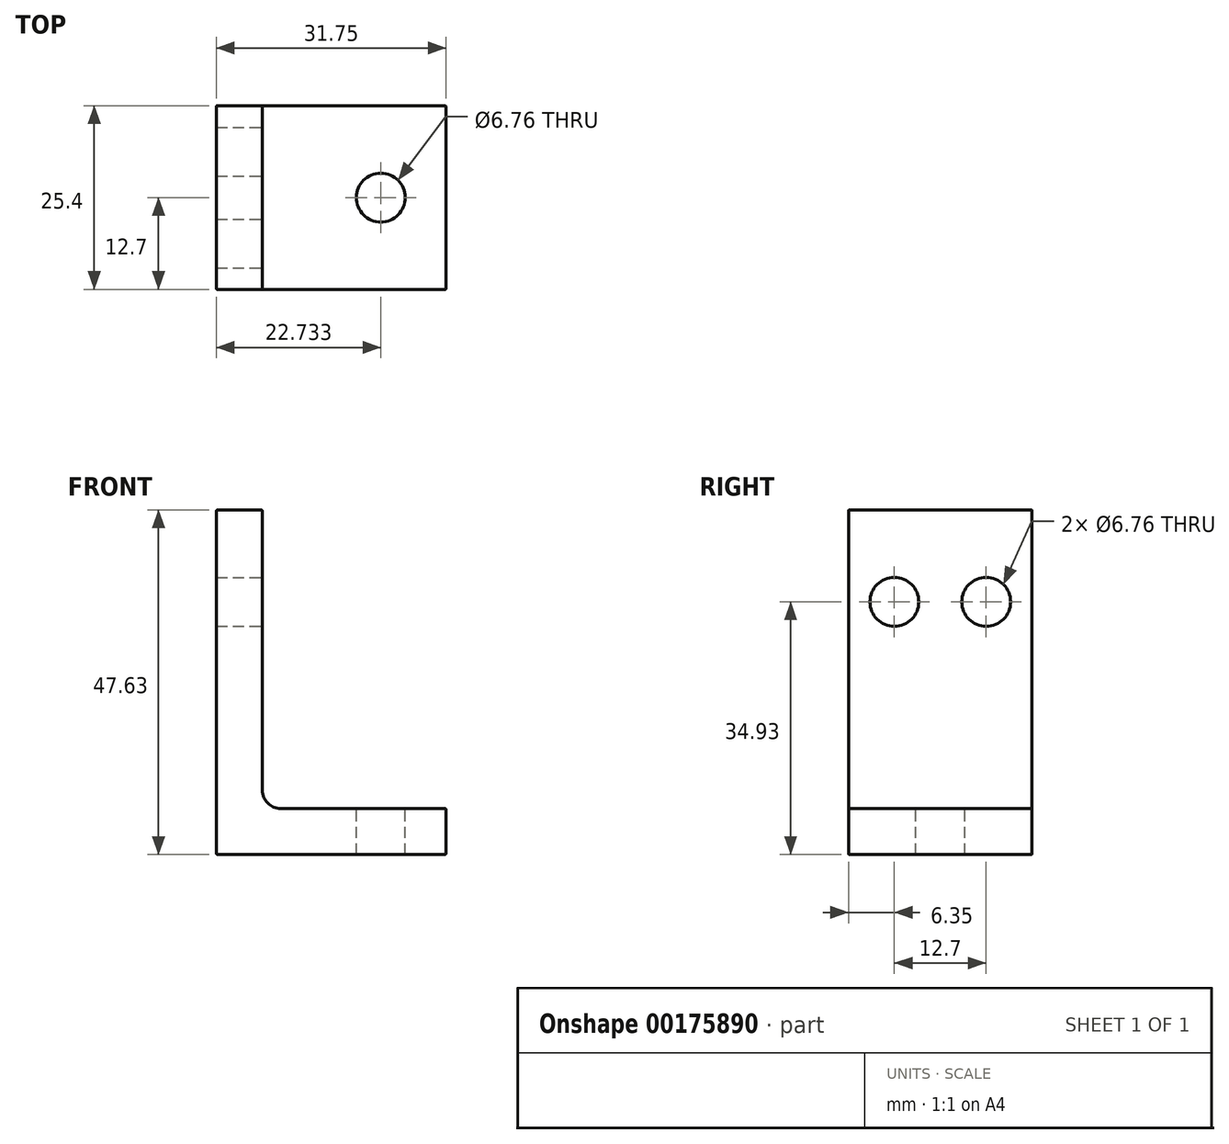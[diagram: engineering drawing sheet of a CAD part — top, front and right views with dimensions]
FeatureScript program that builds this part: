
annotation { "Feature Type Name" : "Feature", "Feature Type Description" : "" }
export const myFeature = defineFeature(function(context is Context, id is Id, definition is map)
    precondition{}
    {
        {
            var Q0;
            Q0=qCreatedBy(makeId("Front.planeOp"),FACE);
            var sketch = newSketch(context, id + "F0", { "sketchPlane" : qUnion([Q0])});
            skLineSegment(sketch, "E0.top", {"start": v(0, 44.45) * mm, "end": v(6.35, 44.45) * mm});
            skLineSegment(sketch, "E0.left", {"start": v(0, 0) * mm, "end": v(0, 44.45) * mm});
            skLineSegment(sketch, "E0.right", {"start": v(6.35, 3.18) * mm, "end": v(6.35, 44.45) * mm});
            skLineSegment(sketch, "E1.bottom", {"start": v(6.35, 3.18) * mm, "end": v(31.75, 3.18) * mm});
            skLineSegment(sketch, "E1.top", {"start": v(0, -3.18) * mm, "end": v(31.75, -3.18) * mm});
            skLineSegment(sketch, "E1.left", {"start": v(0, 3.18) * mm, "end": v(0, -3.18) * mm});
            skLineSegment(sketch, "E1.right", {"start": v(31.75, 3.18) * mm, "end": v(31.75, -3.18) * mm});
            skSolve(sketch);
        }
        {
            var Q0;
            Q0 = qSketchRegion(id + "F0", true);
            extrude(context, id + "F1", {"entities" : qUnion([Q0]), "endBound" : BoundingType.SYMMETRIC, "depth" : 25.4 * mm});
        }
        {
            var Q0;
            Q0=makeQuery(id+"F1.opExtrude","SWEPT_EDGE",EDGE,{"disambiguationData":[OSD([sQuery(id+"F0.wireOp",EDGE,"E0.right"),sQuery(id+"F0.wireOp",EDGE,"E1.bottom")])]});
            fillet(context, id + "F2", {"entities" : qUnion([Q0]), "radius" : 2.54 * mm, "tangentPropagation" : true, "allowEdgeOverflow" : false});
        }
        {
            var Q0;
            Q0=makeQuery(id+"F1.opExtrude","SWEPT_EDGE",EDGE,{"disambiguationData":[OSD([sQuery(id+"F0.wireOp",EDGE,"E0.top"),sQuery(id+"F0.wireOp",EDGE,"E0.right")])]});
            var Q1;
            Q1=makeQuery(id+"F1.opExtrude","SWEPT_EDGE",EDGE,{"disambiguationData":[OSD([sQuery(id+"F0.wireOp",EDGE,"E0.top"),sQuery(id+"F0.wireOp",EDGE,"E0.left")])]});
            var Q2;
            Q2=makeQuery(id+"F1.opExtrude","CAP_EDGE",EDGE,{"disambiguationData":[OSD([sQuery(id+"F0.wireOp",EDGE,"E0.top")])],"isStart":false});
            var Q3;
            Q3=makeQuery(id+"F1.opExtrude","CAP_EDGE",EDGE,{"disambiguationData":[OSD([sQuery(id+"F0.wireOp",EDGE,"E0.right")])],"isStart":false});
            var Q4;
            Q4=makeQuery(id+"F1.opExtrude","CAP_EDGE",EDGE,{"disambiguationData":[OSD([sQuery(id+"F0.wireOp",EDGE,"E1.bottom")])],"isStart":false});
            var Q5;
            Q5=makeQuery(id+"F1.opExtrude","CAP_EDGE",EDGE,{"disambiguationData":[OSD([sQuery(id+"F0.wireOp",EDGE,"E1.top")])],"isStart":false});
            var Q6;
            Q6=makeQuery(id+"F1.opExtrude","CAP_EDGE",EDGE,{"disambiguationData":[OSD([sQuery(id+"F0.wireOp",EDGE,"E0.left"),sQuery(id+"F0.wireOp",EDGE,"E1.left")])],"isStart":false});
            var Q7;
            Q7=makeQuery(id+"F1.opExtrude","SWEPT_EDGE",EDGE,{"disambiguationData":[OSD([sQuery(id+"F0.wireOp",EDGE,"E1.bottom"),sQuery(id+"F0.wireOp",EDGE,"E1.right")])]});
            var Q8;
            Q8=makeQuery(id+"F1.opExtrude","SWEPT_EDGE",EDGE,{"disambiguationData":[OSD([sQuery(id+"F0.wireOp",EDGE,"E1.top"),sQuery(id+"F0.wireOp",EDGE,"E1.right")])]});
            var Q9;
            Q9=makeQuery(id+"F1.opExtrude","CAP_EDGE",EDGE,{"disambiguationData":[OSD([sQuery(id+"F0.wireOp",EDGE,"E1.bottom")])],"isStart":true});
            var Q10;
            Q10=makeQuery(id+"F1.opExtrude","CAP_EDGE",EDGE,{"disambiguationData":[OSD([sQuery(id+"F0.wireOp",EDGE,"E1.right")])],"isStart":true});
            var Q11;
            Q11=makeQuery(id+"F1.opExtrude","CAP_EDGE",EDGE,{"disambiguationData":[OSD([sQuery(id+"F0.wireOp",EDGE,"E1.top")])],"isStart":true});
            var Q12;
            Q12=makeQuery(id+"F1.opExtrude","CAP_EDGE",EDGE,{"disambiguationData":[OSD([sQuery(id+"F0.wireOp",EDGE,"E0.left"),sQuery(id+"F0.wireOp",EDGE,"E1.left")])],"isStart":true});
            var Q13;
            Q13=makeQuery(id+"F1.opExtrude","CAP_EDGE",EDGE,{"disambiguationData":[OSD([sQuery(id+"F0.wireOp",EDGE,"E0.right")])],"isStart":true});
            var Q14;
            Q14=makeQuery(id+"F1.opExtrude","SWEPT_EDGE",EDGE,{"disambiguationData":[OSD([sQuery(id+"F0.wireOp",EDGE,"E1.top"),sQuery(id+"F0.wireOp",EDGE,"E1.left")])]});
            var Q15;
            Q15=makeQuery(id+"F1.opExtrude","CAP_EDGE",EDGE,{"disambiguationData":[OSD([sQuery(id+"F0.wireOp",EDGE,"E1.right")])],"isStart":false});
            var Q16;
            Q16=makeQuery(id+"F1.opExtrude","CAP_EDGE",EDGE,{"disambiguationData":[OSD([sQuery(id+"F0.wireOp",EDGE,"E0.top")])],"isStart":true});
            fillet(context, id + "F3", {"entities" : qUnion([Q0, Q1, Q2, Q3, Q4, Q5, Q6, Q7, Q8, Q9, Q10, Q11, Q12, Q13, Q14, Q15, Q16]), "radius" : 0.13 * mm, "tangentPropagation" : true, "allowEdgeOverflow" : false});
        }
        {
            var Q0;
            Q0=makeQuery(id+"F1.opExtrude","SWEPT_FACE",FACE,{"disambiguationData":[OSD([sQuery(id+"F0.wireOp",EDGE,"E0.right")])]});
            var sketch = newSketch(context, id + "F4", { "sketchPlane" : qUnion([Q0])});
            skCircle(sketch, "E2", {"center": v(-6.35, 31.75) * mm, "radius": 3.38 * mm});
            skCircle(sketch, "E3", {"center": v(6.35, 31.75) * mm, "radius": 3.38 * mm});
            skSolve(sketch);
        }
        {
            var Q0;
            Q0 = qSketchRegion(id + "F4", true);
            extrude(context, id + "F5", {"entities" : qUnion([Q0]), "operationType" : NewBodyOperationType.REMOVE, "endBound" : BoundingType.THROUGH_ALL, "oppositeDirection" : true, "depth" : 25.4 * mm});
        }
        {
            var Q0;
            Q0=makeQuery(id+"F1.opExtrude","SWEPT_FACE",FACE,{"disambiguationData":[OSD([sQuery(id+"F0.wireOp",EDGE,"E1.bottom")])]});
            var sketch = newSketch(context, id + "F6", { "sketchPlane" : qUnion([Q0])});
            skCircle(sketch, "E4", {"center": v(22.73, 0) * mm, "radius": 3.38 * mm});
            skSolve(sketch);
        }
        {
            var Q0;
            Q0 = qSketchRegion(id + "F6", true);
            extrude(context, id + "F7", {"entities" : qUnion([Q0]), "operationType" : NewBodyOperationType.REMOVE, "endBound" : BoundingType.THROUGH_ALL, "oppositeDirection" : true, "depth" : 25.4 * mm});
        }
    });
